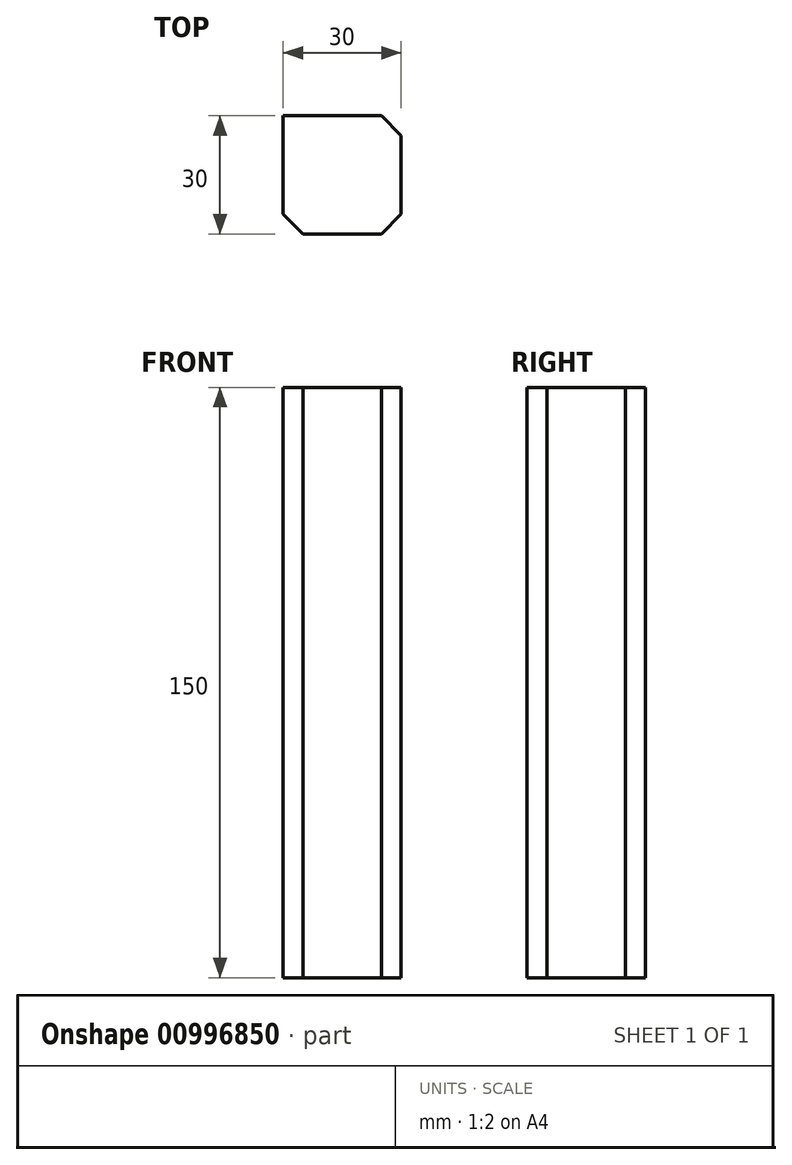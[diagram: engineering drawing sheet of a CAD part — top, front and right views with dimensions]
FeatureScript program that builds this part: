
annotation { "Feature Type Name" : "Feature", "Feature Type Description" : "" }
export const myFeature = defineFeature(function(context is Context, id is Id, definition is map)
    precondition{}
    {
        {
            var Q0;
            Q0=qCreatedBy(makeId("Top.planeOp"),FACE);
            var sketch = newSketch(context, id + "F0", { "sketchPlane" : qUnion([Q0])});
            skLineSegment(sketch, "E0.bottom", {"start": v(0, 0) * mm, "end": v(30, 0) * mm});
            skLineSegment(sketch, "E0.top", {"start": v(0, 30) * mm, "end": v(30, 30) * mm});
            skLineSegment(sketch, "E0.left", {"start": v(0, 0) * mm, "end": v(0, 30) * mm});
            skLineSegment(sketch, "E0.right", {"start": v(30, 0) * mm, "end": v(30, 30) * mm});
            skSolve(sketch);
        }
        {
            var Q0;
            Q0 = qSketchRegion(id + "F0", true);
            extrude(context, id + "F1", {"entities" : qUnion([Q0]), "oppositeDirection" : true, "depth" : 150 * mm, "offsetDistance" : 25 * mm});
        }
        {
            var Q0;
            Q0=makeQuery(id+"F1.opExtrude","SWEPT_EDGE",EDGE,{"disambiguationData":[OSD([sQuery(id+"F0.wireOp",EDGE,"E0.top"),sQuery(id+"F0.wireOp",EDGE,"E0.right")])]});
            var Q1;
            Q1=makeQuery(id+"F1.opExtrude","SWEPT_EDGE",EDGE,{"disambiguationData":[OSD([sQuery(id+"F0.wireOp",EDGE,"E0.bottom"),sQuery(id+"F0.wireOp",EDGE,"E0.right")])]});
            var Q2;
            Q2=makeQuery(id+"F1.opExtrude","SWEPT_EDGE",EDGE,{"disambiguationData":[OSD([sQuery(id+"F0.wireOp",EDGE,"E0.bottom"),sQuery(id+"F0.wireOp",EDGE,"E0.left")])]});
            chamfer(context, id + "F2", {"entities" : qUnion([Q0, Q1, Q2]), "width" : 5 * mm, "tangentPropagation" : true});
        }
    });
